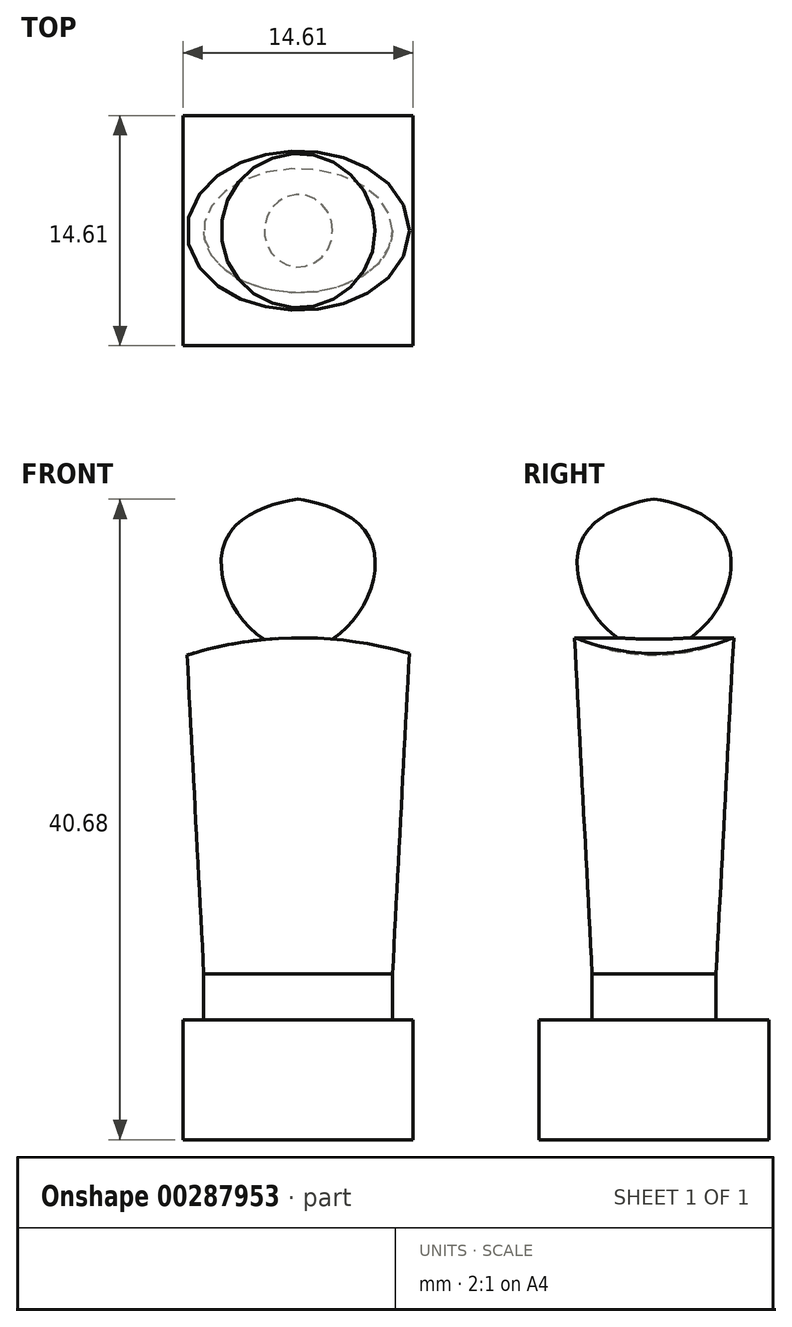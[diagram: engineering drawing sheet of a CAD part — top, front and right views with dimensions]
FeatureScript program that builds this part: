
annotation { "Feature Type Name" : "Feature", "Feature Type Description" : "" }
export const myFeature = defineFeature(function(context is Context, id is Id, definition is map)
    precondition{}
    {
        {
            var Q0;
            Q0=qCreatedBy(makeId("Top.planeOp"),FACE);
            var sketch = newSketch(context, id + "F0", { "sketchPlane" : qUnion([Q0])});
            skLineSegment(sketch, "E0.bottom", {"start": v(-50.86, 28.73) * mm, "end": v(-36.25, 28.73) * mm});
            skLineSegment(sketch, "E0.top", {"start": v(-50.86, 43.34) * mm, "end": v(-36.25, 43.34) * mm});
            skLineSegment(sketch, "E0.left", {"start": v(-50.86, 28.73) * mm, "end": v(-50.86, 43.34) * mm});
            skLineSegment(sketch, "E0.right", {"start": v(-36.25, 28.73) * mm, "end": v(-36.25, 43.34) * mm});
            skSolve(sketch);
        }
        {
            var Q0;
            Q0=makeQuery(id+"F0.imprint","IMPRINT",FACE,{"disambiguationData":[TD([[makeQuery(id+"F0.imprint","IMPRINT",EDGE,{"derivedFrom":sQuery(id+"F0.wireOp",EDGE,"E0.bottom")}),1.0]])]});
            extrude(context, id + "F1", {"entities" : qUnion([Q0]), "depth" : 7.62 * mm});
        }
        {
            var Q0;
            Q0=makeQuery(id+"F1.opExtrude","CAP_FACE",FACE,{"disambiguationData":[OSD([sQuery(id+"F0.wireOp",EDGE,"E0.bottom"),sQuery(id+"F0.wireOp",EDGE,"E0.top"),sQuery(id+"F0.wireOp",EDGE,"E0.left"),sQuery(id+"F0.wireOp",EDGE,"E0.right")])],"isStart":false});
            var sketch = newSketch(context, id + "F2", { "sketchPlane" : qUnion([Q0])});
            skEllipse(sketch, "E1", {"center": v(-43.55, 36.04) * mm, "majorRadius": 6 * mm, "minorRadius": 3.94 * mm, "majorAxis": v(1, 0)});
            skSolve(sketch);
        }
        {
            var Q0;
            Q0=makeQuery(id+"F2.imprint","IMPRINT",FACE,{"disambiguationData":[TD([[makeQuery(id+"F2.imprint","IMPRINT",EDGE,{"derivedFrom":sQuery(id+"F2.wireOp",EDGE,"E1")}),1.0]])]});
            extrude(context, id + "F3", {"entities" : qUnion([Q0]), "operationType" : NewBodyOperationType.ADD, "depth" : 2.92 * mm});
        }
        {
            var Q0;
            Q0=makeQuery(id+"F3.opExtrude","CAP_FACE",FACE,{"disambiguationData":[OSD([sQuery(id+"F2.wireOp",EDGE,"E1")])],"isStart":false});
            var sketch = newSketch(context, id + "F4", { "sketchPlane" : qUnion([Q0])});
            skFitSpline(sketch, "E2.0", {"points": [v(-36.4, 34.88) * mm, v(-36.23, 36.04) * mm, v(-36.4, 37.2) * mm, v(-36.9, 38.24) * mm, v(-37.65, 39.16) * mm, v(-38.6, 39.9) * mm, v(-39.69, 40.5) * mm, v(-40.92, 40.93) * mm, v(-42.2, 41.18) * mm, v(-43.55, 41.27) * mm, v(-44.9, 41.18) * mm, v(-46.19, 40.93) * mm, v(-47.42, 40.5) * mm, v(-48.51, 39.9) * mm, v(-49.46, 39.16) * mm, v(-50.2, 38.24) * mm, v(-50.7, 37.2) * mm, v(-50.88, 36.04) * mm, v(-50.7, 34.88) * mm, v(-50.2, 33.83) * mm, v(-49.46, 32.91) * mm, v(-48.51, 32.16) * mm, v(-47.42, 31.57) * mm, v(-46.19, 31.14) * mm, v(-44.9, 30.89) * mm, v(-43.55, 30.8) * mm, v(-42.2, 30.89) * mm, v(-40.92, 31.14) * mm, v(-39.69, 31.57) * mm, v(-38.6, 32.16) * mm, v(-37.65, 32.91) * mm, v(-36.9, 33.83) * mm, v(-36.4, 34.88) * mm, v(-36.23, 36.04) * mm, v(-36.4, 37.2) * mm, v(-36.4, 34.88) * mm]});
            skSolve(sketch);
        }
        {
            var Q0;
            Q0=makeQuery(id+"F4.imprint","IMPRINT",FACE,{"disambiguationData":[TD([[makeQuery(id+"F4.imprint","IMPRINT",EDGE,{"derivedFrom":sQuery(id+"F4.wireOp",EDGE,"E2.0")}),1.0]])]});
            var Q1;
            Q1=makeQuery(id+"F4.imprint","IMPRINT",FACE,{"disambiguationData":[TD([[makeQuery(id+"F4.imprint","IMPRINT",EDGE,{"derivedFrom":makeQuery(id+"F3.opExtrude","CAP_EDGE",EDGE,{"disambiguationData":[OSD([sQuery(id+"F2.wireOp",EDGE,"E1")])],"isStart":false})}),1.0]])]});
            extrude(context, id + "F5", {"entities" : qUnion([Q0, Q1]), "operationType" : NewBodyOperationType.ADD, "depth" : 21.34 * mm, "hasDraft" : true, "draftAngle" : 3 * degree});
        }
        {
            var Q0;
            Q0=makeQuery(id+"F5.opExtrude","CAP_FACE",FACE,{"disambiguationData":[OSD([sQuery(id+"F4.wireOp",EDGE,"E2.0")])],"isStart":false});
            var sketch = newSketch(context, id + "F6", { "sketchPlane" : qUnion([Q0])});
            skLineSegment(sketch, "E3", {"start": v(-43.55, 47.98) * mm, "end": v(-43.55, 22.5) * mm, "construction": true});
            skLineSegment(sketch, "E4", {"start": v(-57.93, 36.02) * mm, "end": v(-22.35, 36.02) * mm, "construction": true});
            skPoint(sketch, "E5", {"position": v(-43.55, 36.02) * mm});
            skSolve(sketch);
        }
        {
            var Q0;
            Q0=makeQuery(id+"F1.opExtrude","SWEPT_FACE",FACE,{"disambiguationData":[OSD([sQuery(id+"F0.wireOp",EDGE,"E0.bottom")])]});
            var Q1;
            Q1=makeQuery(id+"F1.opExtrude","SWEPT_FACE",FACE,{"disambiguationData":[OSD([sQuery(id+"F0.wireOp",EDGE,"E0.top")])]});
            cPlane(context, id + "F7", {"entities" : qUnion([Q0, Q1]), "cplaneType" : CPlaneType.MID_PLANE, "offset" : 25.4 * mm, "width" : 152.4 * mm, "height" : 152.4 * mm});
        }
        {
            var Q0;
            Q0=qCreatedBy(id+"F7.planeOp",FACE);
            var sketch = newSketch(context, id + "F8", { "sketchPlane" : qUnion([Q0])});
            skLineSegment(sketch, "E6", {"start": v(-43.55, 41.6) * mm, "end": v(-43.55, -24.22) * mm, "construction": true});
            skSolve(sketch);
        }
        {
            var Q0;
            Q0=qCreatedBy(id+"F7.planeOp",FACE);
            var sketch = newSketch(context, id + "F9", { "sketchPlane" : qUnion([Q0])});
            skArc(sketch, "E7", {"start": v(-27.53, 26) * mm, "mid": v(-43.12, 31.88) * mm, "end": v(-58.84, 26.34) * mm});
            skLineSegment(sketch, "E8", {"start": v(-50.86, 0) * mm, "end": v(-58.84, 26.34) * mm});
            skLineSegment(sketch, "E9", {"start": v(-27.53, 26) * mm, "end": v(-36.25, 0) * mm});
            skLineSegment(sketch, "E10", {"start": v(-36.25, 0) * mm, "end": v(-50.86, 0) * mm});
            skSolve(sketch);
        }
        {
            var Q0;
            Q0=makeQuery(id+"F9.imprint","IMPRINT",FACE,{"disambiguationData":[TD([[makeQuery(id+"F9.imprint","IMPRINT",EDGE,{"derivedFrom":sQuery(id+"F9.wireOp",EDGE,"E7")}),1.0]])]});
            extrude(context, id + "F10", {"entities" : qUnion([Q0]), "operationType" : NewBodyOperationType.INTERSECT, "depth" : 25.4 * mm, "hasSecondDirection" : true, "secondDirectionOppositeDirection" : true, "secondDirectionDepth" : 25.4 * mm});
        }
        {
            var Q0;
            Q0=qCreatedBy(id+"F7.planeOp",FACE);
            var sketch = newSketch(context, id + "F11", { "sketchPlane" : qUnion([Q0])});
            skLineSegment(sketch, "E11", {"start": v(-43.55, 30.9) * mm, "end": v(-43.55, 40.68) * mm});
            skFitSpline(sketch, "E12", {"points": [v(-43.55, 40.68) * mm, v(-39.41, 38.82) * mm, v(-39.32, 34.1) * mm, v(-43.55, 30.9) * mm], "startDerivative": vector(8.61, -0.76) * mm, "endDerivative": vector(-14.99, -2.36) * mm});
            skSolve(sketch);
        }
        {
            var Q0;
            Q0=makeQuery(id+"F11.imprint","IMPRINT",FACE,{"disambiguationData":[TD([[makeQuery(id+"F11.imprint","IMPRINT",EDGE,{"derivedFrom":sQuery(id+"F11.wireOp",EDGE,"E11")}),-1.0]])]});
            var Q1;
            Q1=sQuery(id+"F11.wireOp",EDGE,"E11");
            revolve(context, id + "F12", {"operationType" : NewBodyOperationType.ADD, "entities" : qUnion([Q0]), "axis" : qUnion([Q1]), "revolveType" : RevolveType.FULL});
        }
    });
